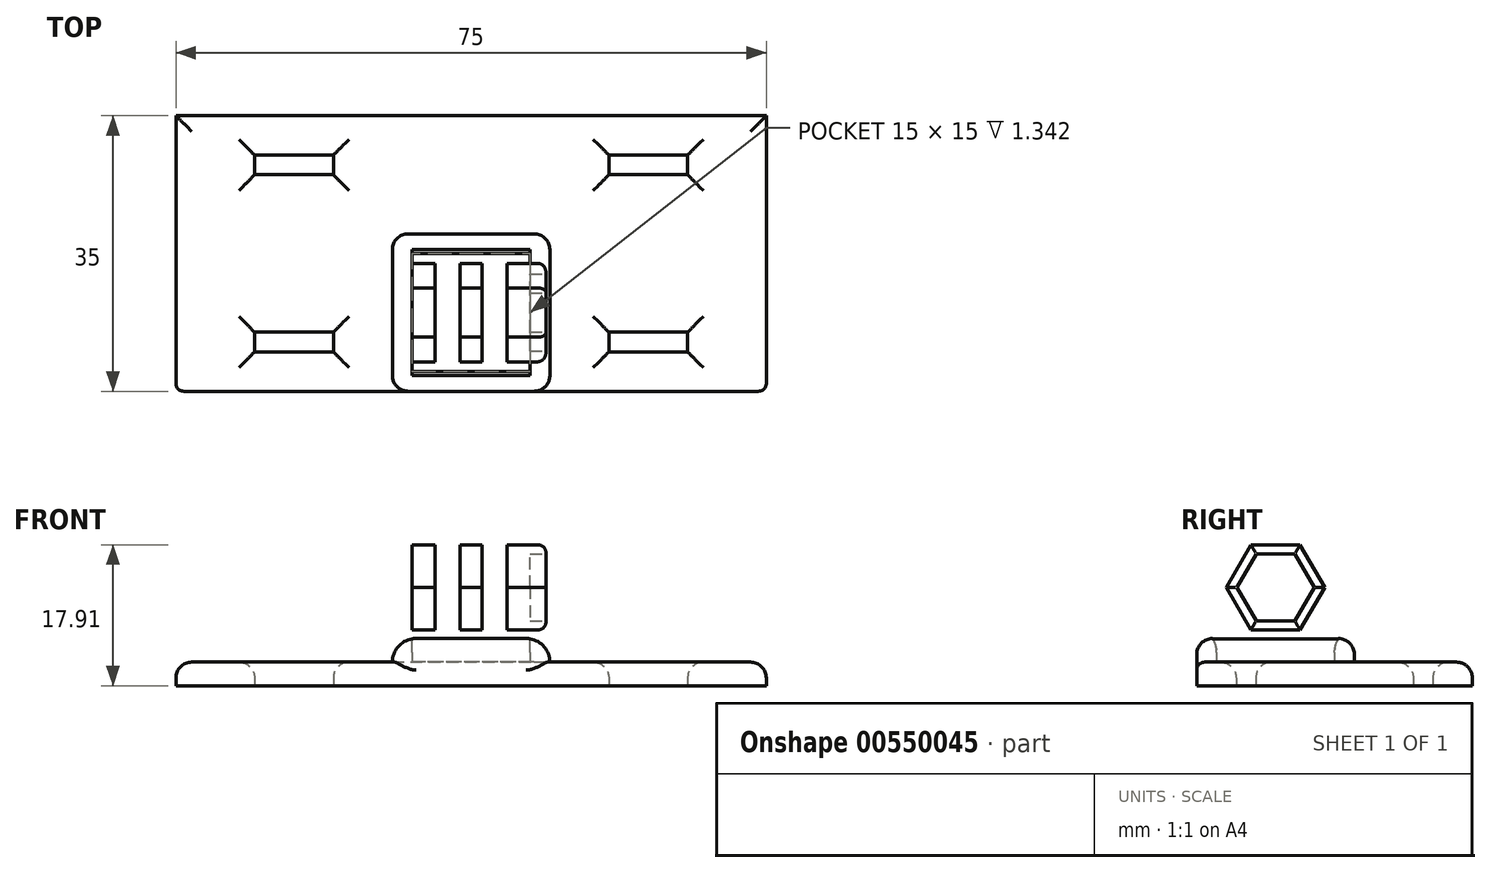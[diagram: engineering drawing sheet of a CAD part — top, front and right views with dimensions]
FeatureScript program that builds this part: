
annotation { "Feature Type Name" : "Feature", "Feature Type Description" : "" }
export const myFeature = defineFeature(function(context is Context, id is Id, definition is map)
    precondition{}
    {
        {
            var Q0;
            Q0=qCreatedBy(makeId("Right.planeOp"),FACE);
            var sketch = newSketch(context, id + "F0", { "sketchPlane" : qUnion([Q0])});
            skPoint(sketch, "E0", {"position": v(0, 12.5) * mm});
            skPoint(sketch, "E1", {"position": v(7.5, 0) * mm});
            skPoint(sketch, "E2.end.orphan", {"position": v(-7.5, 0) * mm});
            skLineSegment(sketch, "E3.top", {"start": v(-7.5, 0) * mm, "end": v(7.5, 0) * mm});
            skLineSegment(sketch, "E3.left", {"start": v(-7.5, 12.5) * mm, "end": v(-7.5, 0) * mm});
            skLineSegment(sketch, "E3.right", {"start": v(7.5, 12.5) * mm, "end": v(7.5, 0) * mm});
            skArc(sketch, "E4", {"start": v(7.5, 12.5) * mm, "mid": v(0, 20) * mm, "end": v(-7.5, 12.5) * mm});
            skCircle(sketch, "E5.cCircle", {"center": v(0, 12.5) * mm, "radius": 4.25 * mm, "construction": true});
            skLineSegment(sketch, "E5.0", {"start": v(-2.45, 16.75) * mm, "end": v(2.45, 16.75) * mm});
            skLineSegment(sketch, "E5.1", {"start": v(2.45, 16.75) * mm, "end": v(4.9, 12.5) * mm});
            skLineSegment(sketch, "E5.2", {"start": v(4.9, 12.5) * mm, "end": v(2.45, 8.25) * mm});
            skLineSegment(sketch, "E5.3", {"start": v(2.45, 8.25) * mm, "end": v(-2.45, 8.25) * mm});
            skLineSegment(sketch, "E5.4", {"start": v(-2.45, 8.25) * mm, "end": v(-4.9, 12.5) * mm});
            skLineSegment(sketch, "E5.5", {"start": v(-4.9, 12.5) * mm, "end": v(-2.45, 16.75) * mm});
            skPoint(sketch, "E5.0.midPoint", {"position": v(0, 16.75) * mm});
            skCircle(sketch, "E6.cCircle", {"center": v(0, 12.5) * mm, "radius": 5.41 * mm, "construction": true});
            skLineSegment(sketch, "E6.0", {"start": v(-3.12, 17.91) * mm, "end": v(3.12, 17.91) * mm});
            skLineSegment(sketch, "E6.1", {"start": v(3.12, 17.91) * mm, "end": v(6.25, 12.5) * mm});
            skLineSegment(sketch, "E6.2", {"start": v(6.25, 12.5) * mm, "end": v(3.12, 7.09) * mm});
            skLineSegment(sketch, "E6.3", {"start": v(3.13, 7.09) * mm, "end": v(-3.12, 7.09) * mm});
            skLineSegment(sketch, "E6.4", {"start": v(-3.12, 7.09) * mm, "end": v(-6.25, 12.5) * mm});
            skLineSegment(sketch, "E6.5", {"start": v(-6.25, 12.5) * mm, "end": v(-3.12, 17.91) * mm});
            skPoint(sketch, "E6.0.midPoint", {"position": v(0, 17.91) * mm});
            skLineSegment(sketch, "E7.top", {"start": v(-7.5, 3) * mm, "end": v(7.5, 3) * mm});
            skLineSegment(sketch, "E7.left", {"start": v(-7.5, 0) * mm, "end": v(-7.5, 3) * mm});
            skLineSegment(sketch, "E7.right", {"start": v(7.5, 0) * mm, "end": v(7.5, 3) * mm});
            skSolve(sketch);
        }
        {
            var Q0;
            Q0=makeQuery(id+"F0.imprint","IMPRINT",FACE,{"disambiguationData":[TD([[makeQuery(id+"F0.imprint","IMPRINT",EDGE,{"derivedFrom":sQuery(id+"F0.wireOp",EDGE,"E3.top")}),1.0]])]});
            extrude(context, id + "F1", {"entities" : qUnion([Q0]), "oppositeDirection" : true, "depth" : 15 * mm, "offsetDistance" : 25 * mm});
        }
        {
            var Q0;
            Q0=makeQuery(id+"F0.imprint","IMPRINT",FACE,{"disambiguationData":[TD([[makeQuery(id+"F0.imprint","IMPRINT",EDGE,{"derivedFrom":sQuery(id+"F0.wireOp",EDGE,"E3.left")}),1.0]])]});
            extrude(context, id + "F2", {"entities" : qUnion([Q0]), "operationType" : NewBodyOperationType.ADD, "oppositeDirection" : true, "depth" : 3 * mm, "offsetDistance" : 25 * mm});
        }
        {
            var Q0;
            Q0=makeQuery(id+"F0.imprint","IMPRINT",FACE,{"disambiguationData":[TD([[makeQuery(id+"F0.imprint","IMPRINT",EDGE,{"derivedFrom":sQuery(id+"F0.wireOp",EDGE,"E5.0")}),1.0]])]});
            extrude(context, id + "F3", {"entities" : qUnion([Q0]), "operationType" : NewBodyOperationType.ADD, "oppositeDirection" : true, "depth" : 3 * mm, "offsetDistance" : 25 * mm});
        }
        {
            var Q0;
            Q0=makeQuery(id+"F0.imprint","IMPRINT",FACE,{"disambiguationData":[TD([[makeQuery(id+"F0.imprint","IMPRINT",EDGE,{"derivedFrom":sQuery(id+"F0.wireOp",EDGE,"E5.0")}),1.0]])]});
            extrude(context, id + "F4", {"entities" : qUnion([Q0]), "operationType" : NewBodyOperationType.ADD, "depth" : 2 * mm, "offsetDistance" : 25 * mm});
        }
        {
            var Q0;
            Q0=makeQuery(id+"F0.imprint","IMPRINT",FACE,{"disambiguationData":[TD([[makeQuery(id+"F0.imprint","IMPRINT",EDGE,{"derivedFrom":sQuery(id+"F0.wireOp",EDGE,"E5.0")}),-1.0]])]});
            extrude(context, id + "F5", {"entities" : qUnion([Q0]), "operationType" : NewBodyOperationType.ADD, "oppositeDirection" : true, "depth" : 3 * mm, "offsetDistance" : 25 * mm});
        }
        {
            var Q0;
            {var subQ0=sQuery(id+"F0.wireOp",EDGE,"E5.5");var subQ1=sQuery(id+"F0.wireOp",EDGE,"E5.4");var subQ2=sQuery(id+"F0.wireOp",EDGE,"E5.3");var subQ3=sQuery(id+"F0.wireOp",EDGE,"E5.2");var subQ4=sQuery(id+"F0.wireOp",EDGE,"E5.1");var subQ5=sQuery(id+"F0.wireOp",EDGE,"E5.0");var subQ6=sQuery(id+"F0.wireOp",EDGE,"E6.5");var subQ7=sQuery(id+"F0.wireOp",EDGE,"E6.4");var subQ8=sQuery(id+"F0.wireOp",EDGE,"E6.3");var subQ9=sQuery(id+"F0.wireOp",EDGE,"E6.2");var subQ10=sQuery(id+"F0.wireOp",EDGE,"E6.1");var subQ11=sQuery(id+"F0.wireOp",EDGE,"E6.0");Q0=makeQuery(id+"F5.boolean.opBoolean","MERGE",FACE,{"derivedFrom":[makeQuery(id+"F3.boolean.opBoolean","MERGE",FACE,{"derivedFrom":[makeQuery(id+"F2.opExtrude","CAP_FACE",FACE,{"disambiguationData":[OSD([sQuery(id+"F0.wireOp",EDGE,"E3.left"),sQuery(id+"F0.wireOp",EDGE,"E3.right"),sQuery(id+"F0.wireOp",EDGE,"E4"),subQ11,subQ10,subQ9,subQ8,subQ7,subQ6,sQuery(id+"F0.wireOp",EDGE,"E7.top")])],"isStart":false}),makeQuery(id+"F3.opExtrude","CAP_FACE",FACE,{"disambiguationData":[OSD([subQ5,subQ4,subQ3,subQ2,subQ1,subQ0,subQ11,subQ10,subQ9,subQ8,subQ7,subQ6])],"isStart":false})]}),makeQuery(id+"F5.opExtrude","CAP_FACE",FACE,{"disambiguationData":[OSD([subQ5,subQ4,subQ3,subQ2,subQ1,subQ0])],"isStart":false})]});}
            extrude(context, id + "F6", {"entities" : qUnion([Q0]), "operationType" : NewBodyOperationType.ADD, "depth" : 12 * mm, "offsetDistance" : 25 * mm});
        }
        {
            var Q0;
            Q0=sQuery(id+"F0.wireOp",VERTEX,"E0");
            var Q1;
            Q1=makeQuery(id+"F1.opExtrude","SWEPT_BODY",BODY,{"disambiguationData":[OSD([sQuery(id+"F0.wireOp",EDGE,"E3.top"),sQuery(id+"F0.wireOp",EDGE,"E7.top"),sQuery(id+"F0.wireOp",EDGE,"E7.left"),sQuery(id+"F0.wireOp",EDGE,"E7.right")])]});
            hole(context, id + "F7", {"style" : HoleStyle.SIMPLE, "endStyle" : HoleEndStyle.BLIND, "holeDiameter" : 5 * mm, "holeDepth" : 15 * mm, "locations" : qUnion([Q0]), "scope" : qUnion([Q1])});
        }
        {
            var Q0;
            Q0=qCreatedBy(makeId("Top.planeOp"),FACE);
            cPlane(context, id + "F8", {"entities" : qUnion([Q0]), "cplaneType" : CPlaneType.OFFSET, "offset" : 20 * mm, "width" : 150 * mm, "height" : 150 * mm});
        }
        {
            var Q0;
            Q0=qCreatedBy(id+"F8.planeOp",FACE);
            var sketch = newSketch(context, id + "F9", { "sketchPlane" : qUnion([Q0])});
            skLineSegment(sketch, "E8.top", {"start": v(0, 7.5) * mm, "end": v(-15, 7.5) * mm});
            skLineSegment(sketch, "E8.left", {"start": v(0, 0) * mm, "end": v(0, 7.5) * mm});
            skLineSegment(sketch, "E8.right", {"start": v(-15, 0) * mm, "end": v(-15, 7.5) * mm});
            skLineSegment(sketch, "E9.top", {"start": v(-15, -7.5) * mm, "end": v(0, -7.5) * mm});
            skLineSegment(sketch, "E9.left", {"start": v(-15, 0) * mm, "end": v(-15, -7.5) * mm});
            skLineSegment(sketch, "E9.right", {"start": v(0, 0) * mm, "end": v(0, -7.5) * mm});
            skLineSegment(sketch, "E10", {"start": v(-7.5, -7.5) * mm, "end": v(-7.5, 7.5) * mm, "construction": true});
            skPoint(sketch, "E11", {"position": v(-6.1, -7.5) * mm});
            skLineSegment(sketch, "E12.bottom", {"start": v(-6.1, -7.5) * mm, "end": v(-8.9, -7.5) * mm});
            skLineSegment(sketch, "E12.top", {"start": v(-6.1, 7.5) * mm, "end": v(-8.9, 7.5) * mm});
            skLineSegment(sketch, "E12.left", {"start": v(-6.1, -7.5) * mm, "end": v(-6.1, 7.5) * mm});
            skLineSegment(sketch, "E12.right", {"start": v(-8.9, -7.5) * mm, "end": v(-8.9, 7.5) * mm});
            skLineSegment(sketch, "E13.bottom", {"start": v(-15, -7.5) * mm, "end": v(-12.05, -7.5) * mm});
            skLineSegment(sketch, "E13.top", {"start": v(-15, 7.5) * mm, "end": v(-12.05, 7.5) * mm});
            skLineSegment(sketch, "E13.left", {"start": v(-15, -7.5) * mm, "end": v(-15, 7.5) * mm});
            skLineSegment(sketch, "E13.right", {"start": v(-12.05, -7.5) * mm, "end": v(-12.05, 7.5) * mm});
            skLineSegment(sketch, "E14.bottom", {"start": v(0, -7.5) * mm, "end": v(-2.95, -7.5) * mm});
            skLineSegment(sketch, "E14.top", {"start": v(0, 7.5) * mm, "end": v(-2.95, 7.5) * mm});
            skLineSegment(sketch, "E14.left", {"start": v(0, -7.5) * mm, "end": v(0, 7.5) * mm});
            skLineSegment(sketch, "E14.right", {"start": v(-2.95, -7.5) * mm, "end": v(-2.95, 7.5) * mm});
            skLineSegment(sketch, "E15", {"start": v(-12.05, -7.5) * mm, "end": v(-8.9, -7.5) * mm, "construction": true});
            skSolve(sketch);
        }
        {
            var Q0;
            {var subQ2=sQuery(id+"F9.wireOp",EDGE,"E12.right");Q0=makeQuery(id+"F9.imprint","IMPRINT",FACE,{"disambiguationData":[TD([[makeQuery(id+"F9.imprint","IMPRINT",EDGE,{"derivedFrom":subQ2}),1.0]])]});}
            var Q1;
            {var subQ2=sQuery(id+"F9.wireOp",EDGE,"E12.left");Q1=makeQuery(id+"F9.imprint","IMPRINT",FACE,{"disambiguationData":[TD([[makeQuery(id+"F9.imprint","IMPRINT",EDGE,{"derivedFrom":subQ2}),-1.0]])]});}
            extrude(context, id + "F10", {"entities" : qUnion([Q0, Q1]), "operationType" : NewBodyOperationType.REMOVE, "oppositeDirection" : true, "depth" : 17 * mm, "offsetDistance" : 25 * mm});
        }
        {
            var Q0;
            Q0=makeQuery(id+"F4.opExtrude","CAP_EDGE",EDGE,{"disambiguationData":[OSD([sQuery(id+"F0.wireOp",EDGE,"E6.4")])],"isStart":false});
            var Q1;
            Q1=makeQuery(id+"F4.opExtrude","CAP_EDGE",EDGE,{"disambiguationData":[OSD([sQuery(id+"F0.wireOp",EDGE,"E6.3")])],"isStart":false});
            var Q2;
            Q2=makeQuery(id+"F4.opExtrude","CAP_EDGE",EDGE,{"disambiguationData":[OSD([sQuery(id+"F0.wireOp",EDGE,"E6.5")])],"isStart":false});
            var Q3;
            Q3=makeQuery(id+"F4.opExtrude","CAP_EDGE",EDGE,{"disambiguationData":[OSD([sQuery(id+"F0.wireOp",EDGE,"E6.0")])],"isStart":false});
            var Q4;
            Q4=makeQuery(id+"F4.opExtrude","CAP_EDGE",EDGE,{"disambiguationData":[OSD([sQuery(id+"F0.wireOp",EDGE,"E6.1")])],"isStart":false});
            var Q5;
            Q5=makeQuery(id+"F4.opExtrude","CAP_EDGE",EDGE,{"disambiguationData":[OSD([sQuery(id+"F0.wireOp",EDGE,"E6.2")])],"isStart":false});
            fillet(context, id + "F11", {"entities" : qUnion([Q0, Q1, Q2, Q3, Q4, Q5]), "radius" : 1 * mm, "tangentPropagation" : true, "allowEdgeOverflow" : false});
        }
        {
            var Q0;
            Q0=makeQuery(id+"F1.opExtrude","SWEPT_FACE",FACE,{"disambiguationData":[OSD([sQuery(id+"F0.wireOp",EDGE,"E3.top")])]});
            var sketch = newSketch(context, id + "F12", { "sketchPlane" : qUnion([Q0])});
            skLineSegment(sketch, "E16", {"start": v(0, 0) * mm, "end": v(-15, 0) * mm, "construction": true});
            skLineSegment(sketch, "E17.bottom", {"start": v(-7.5, 0) * mm, "end": v(30, 0) * mm});
            skLineSegment(sketch, "E17.top", {"start": v(-7.5, -25) * mm, "end": v(30, -25) * mm});
            skLineSegment(sketch, "E17.left", {"start": v(-7.5, 0) * mm, "end": v(-7.5, -25) * mm, "construction": true});
            skLineSegment(sketch, "E17.right", {"start": v(30, 0) * mm, "end": v(30, -25) * mm});
            skLineSegment(sketch, "E18.bottom", {"start": v(-7.5, 0) * mm, "end": v(30, 0) * mm, "construction": true});
            skLineSegment(sketch, "E18.top", {"start": v(-7.5, 10) * mm, "end": v(30, 10) * mm});
            skLineSegment(sketch, "E18.left", {"start": v(-7.5, 0) * mm, "end": v(-7.5, 10) * mm});
            skLineSegment(sketch, "E18.right", {"start": v(30, 0) * mm, "end": v(30, 10) * mm});
            skLineSegment(sketch, "E19.bottom", {"start": v(-7.5, 0) * mm, "end": v(-45, 0) * mm, "construction": true});
            skLineSegment(sketch, "E19.top", {"start": v(-7.5, 10) * mm, "end": v(-45, 10) * mm});
            skLineSegment(sketch, "E19.left", {"start": v(-7.5, 0) * mm, "end": v(-7.5, 10) * mm, "construction": true});
            skLineSegment(sketch, "E19.right", {"start": v(-45, 0) * mm, "end": v(-45, 10) * mm});
            skLineSegment(sketch, "E20.bottom", {"start": v(-7.5, 0) * mm, "end": v(-45, 0) * mm});
            skLineSegment(sketch, "E20.top", {"start": v(-7.5, -25) * mm, "end": v(-45, -25) * mm});
            skLineSegment(sketch, "E20.left", {"start": v(-7.5, 0) * mm, "end": v(-7.5, -25) * mm});
            skLineSegment(sketch, "E20.right", {"start": v(-45, 0) * mm, "end": v(-45, -25) * mm});
            skLineSegment(sketch, "E21", {"start": v(-45, -25) * mm, "end": v(-45, 10) * mm, "construction": true});
            skLineSegment(sketch, "E22", {"start": v(30, 10) * mm, "end": v(-45, 10) * mm, "construction": true});
            skLineSegment(sketch, "E23.bottom", {"start": v(-35, 2.5) * mm, "end": v(-25, 2.5) * mm});
            skLineSegment(sketch, "E23.top", {"start": v(-35, 5) * mm, "end": v(-25, 5) * mm});
            skLineSegment(sketch, "E23.left", {"start": v(-35, 2.5) * mm, "end": v(-35, 5) * mm});
            skLineSegment(sketch, "E23.right", {"start": v(-25, 2.5) * mm, "end": v(-25, 5) * mm});
            skLineSegment(sketch, "E24.bottom", {"start": v(10, 2.5) * mm, "end": v(20, 2.5) * mm});
            skLineSegment(sketch, "E24.top", {"start": v(10, 5) * mm, "end": v(20, 5) * mm});
            skLineSegment(sketch, "E24.left", {"start": v(10, 2.5) * mm, "end": v(10, 5) * mm});
            skLineSegment(sketch, "E24.right", {"start": v(20, 2.5) * mm, "end": v(20, 5) * mm});
            skLineSegment(sketch, "E25.bottom", {"start": v(10, -20) * mm, "end": v(20, -20) * mm});
            skLineSegment(sketch, "E25.top", {"start": v(10, -17.5) * mm, "end": v(20, -17.5) * mm});
            skLineSegment(sketch, "E25.left", {"start": v(10, -20) * mm, "end": v(10, -17.5) * mm});
            skLineSegment(sketch, "E25.right", {"start": v(20, -20) * mm, "end": v(20, -17.5) * mm});
            skLineSegment(sketch, "E26.bottom", {"start": v(-35, -20) * mm, "end": v(-25, -20) * mm});
            skLineSegment(sketch, "E26.top", {"start": v(-35, -17.5) * mm, "end": v(-25, -17.5) * mm});
            skLineSegment(sketch, "E26.left", {"start": v(-35, -20) * mm, "end": v(-35, -17.5) * mm});
            skLineSegment(sketch, "E26.right", {"start": v(-25, -20) * mm, "end": v(-25, -17.5) * mm});
            skLineSegment(sketch, "E27", {"start": v(10, -20) * mm, "end": v(10, -25) * mm, "construction": true});
            skLineSegment(sketch, "E28", {"start": v(-25, -20) * mm, "end": v(-25, -25) * mm, "construction": true});
            skLineSegment(sketch, "E29", {"start": v(10, 5) * mm, "end": v(10, 10) * mm, "construction": true});
            skLineSegment(sketch, "E30", {"start": v(-25, 5) * mm, "end": v(-25, 10) * mm, "construction": true});
            skLineSegment(sketch, "E31", {"start": v(20, -20) * mm, "end": v(30, -20) * mm, "construction": true});
            skLineSegment(sketch, "E32", {"start": v(20, 5) * mm, "end": v(30, 5) * mm, "construction": true});
            skLineSegment(sketch, "E33", {"start": v(-35, 5) * mm, "end": v(-45, 5) * mm, "construction": true});
            skLineSegment(sketch, "E34", {"start": v(-35, -17.5) * mm, "end": v(-45, -17.5) * mm, "construction": true});
            skSolve(sketch);
        }
        {
            var Q0;
            Q0 = qSketchRegion(id + "F12", true);
            extrude(context, id + "F13", {"entities" : qUnion([Q0]), "operationType" : NewBodyOperationType.ADD, "oppositeDirection" : true, "depth" : 3 * mm, "offsetDistance" : 25 * mm});
        }
        {
            var Q0;
            {var subQ0=sQuery(id+"F9.wireOp",EDGE,"E9.top");var subQ1=sQuery(id+"F9.wireOp",EDGE,"E8.top");Q0=makeQuery(id+"F13.boolean.opBoolean","MERGE",FACE,{"derivedFrom":[makeQuery(id+"F10.boolean.opBoolean","COPY",FACE,{"derivedFrom":makeQuery(id+"F10.opExtrude","CAP_FACE",FACE,{"disambiguationData":[OSD([subQ1,subQ0,sQuery(id+"F9.wireOp",EDGE,"E12.left"),sQuery(id+"F9.wireOp",EDGE,"E14.right")])],"isStart":false})}),makeQuery(id+"F10.boolean.opBoolean","COPY",FACE,{"derivedFrom":makeQuery(id+"F10.opExtrude","CAP_FACE",FACE,{"disambiguationData":[OSD([subQ1,subQ0,sQuery(id+"F9.wireOp",EDGE,"E12.right"),sQuery(id+"F9.wireOp",EDGE,"E13.right")])],"isStart":false})}),makeQuery(id+"F13.opExtrude","CAP_FACE",FACE,{"disambiguationData":[OSD([sQuery(id+"F12.wireOp",EDGE,"E17.top"),sQuery(id+"F12.wireOp",EDGE,"E17.right"),sQuery(id+"F12.wireOp",EDGE,"E18.top"),sQuery(id+"F12.wireOp",EDGE,"E18.right"),sQuery(id+"F12.wireOp",EDGE,"E19.top"),sQuery(id+"F12.wireOp",EDGE,"E19.right"),sQuery(id+"F12.wireOp",EDGE,"E20.top"),sQuery(id+"F12.wireOp",EDGE,"E20.right"),sQuery(id+"F12.wireOp",EDGE,"E23.bottom"),sQuery(id+"F12.wireOp",EDGE,"E23.top"),sQuery(id+"F12.wireOp",EDGE,"E23.left"),sQuery(id+"F12.wireOp",EDGE,"E23.right"),sQuery(id+"F12.wireOp",EDGE,"E24.bottom"),sQuery(id+"F12.wireOp",EDGE,"E24.top"),sQuery(id+"F12.wireOp",EDGE,"E24.left"),sQuery(id+"F12.wireOp",EDGE,"E24.right"),sQuery(id+"F12.wireOp",EDGE,"E25.bottom"),sQuery(id+"F12.wireOp",EDGE,"E25.top"),sQuery(id+"F12.wireOp",EDGE,"E25.left"),sQuery(id+"F12.wireOp",EDGE,"E25.right"),sQuery(id+"F12.wireOp",EDGE,"E26.bottom"),sQuery(id+"F12.wireOp",EDGE,"E26.top"),sQuery(id+"F12.wireOp",EDGE,"E26.left"),sQuery(id+"F12.wireOp",EDGE,"E26.right"),sQuery(id+"F12.wireOp",EDGE,"uoogrX0K-hDYU-zlST-xG9k-PASHNL5tbvwQ.bottom"),sQuery(id+"F12.wireOp",EDGE,"uoogrX0K-hDYU-zlST-xG9k-PASHNL5tbvwQ.top"),sQuery(id+"F12.wireOp",EDGE,"uoogrX0K-hDYU-zlST-xG9k-PASHNL5tbvwQ.left"),sQuery(id+"F12.wireOp",EDGE,"uoogrX0K-hDYU-zlST-xG9k-PASHNL5tbvwQ.right"),sQuery(id+"F12.wireOp",EDGE,"PsY2hvwu-Xq4P-Rnf6-JxBB-JTYvY8m7WrV5.bottom"),sQuery(id+"F12.wireOp",EDGE,"PsY2hvwu-Xq4P-Rnf6-JxBB-JTYvY8m7WrV5.top"),sQuery(id+"F12.wireOp",EDGE,"PsY2hvwu-Xq4P-Rnf6-JxBB-JTYvY8m7WrV5.left"),sQuery(id+"F12.wireOp",EDGE,"PsY2hvwu-Xq4P-Rnf6-JxBB-JTYvY8m7WrV5.right")])],"isStart":false})]});}
            var sketch = newSketch(context, id + "F14", { "sketchPlane" : qUnion([Q0])});
            skLineSegment(sketch, "E35.bottom", {"start": v(2.5, 10) * mm, "end": v(-2.95, 10) * mm});
            skLineSegment(sketch, "E35.top", {"start": v(2.5, 7.5) * mm, "end": v(-2.95, 7.5) * mm});
            skLineSegment(sketch, "E35.left", {"start": v(2.5, 10) * mm, "end": v(2.5, 7.5) * mm});
            skLineSegment(sketch, "E35.right", {"start": v(-2.95, 10) * mm, "end": v(-2.95, 7.5) * mm});
            skLineSegment(sketch, "E36.bottom", {"start": v(-6.1, 7.5) * mm, "end": v(-8.9, 7.5) * mm});
            skLineSegment(sketch, "E36.top", {"start": v(-6.1, 10) * mm, "end": v(-8.9, 10) * mm});
            skLineSegment(sketch, "E36.left", {"start": v(-6.1, 7.5) * mm, "end": v(-6.1, 10) * mm});
            skLineSegment(sketch, "E36.right", {"start": v(-8.9, 7.5) * mm, "end": v(-8.9, 10) * mm});
            skLineSegment(sketch, "E37.bottom", {"start": v(-12.05, 10) * mm, "end": v(-17.5, 10) * mm});
            skLineSegment(sketch, "E37.top", {"start": v(-12.05, 7.5) * mm, "end": v(-17.5, 7.5) * mm});
            skLineSegment(sketch, "E37.left", {"start": v(-12.05, 10) * mm, "end": v(-12.05, 7.5) * mm});
            skLineSegment(sketch, "E37.right", {"start": v(-17.5, 10) * mm, "end": v(-17.5, 7.5) * mm});
            skLineSegment(sketch, "E38", {"start": v(-12.05, 10) * mm, "end": v(-8.9, 10) * mm, "construction": true});
            skLineSegment(sketch, "E39.bottom", {"start": v(2.5, 7.5) * mm, "end": v(0, 7.5) * mm});
            skLineSegment(sketch, "E39.top", {"start": v(2.5, -7.5) * mm, "end": v(0, -7.5) * mm});
            skLineSegment(sketch, "E39.left", {"start": v(2.5, 7.5) * mm, "end": v(2.5, -7.5) * mm});
            skLineSegment(sketch, "E39.right", {"start": v(0, 7.5) * mm, "end": v(0, -7.5) * mm});
            skLineSegment(sketch, "E40.bottom", {"start": v(-17.5, 7.5) * mm, "end": v(-15, 7.5) * mm});
            skLineSegment(sketch, "E40.top", {"start": v(-17.5, -7.5) * mm, "end": v(-15, -7.5) * mm});
            skLineSegment(sketch, "E40.left", {"start": v(-17.5, 7.5) * mm, "end": v(-17.5, -7.5) * mm});
            skLineSegment(sketch, "E40.right", {"start": v(-15, 7.5) * mm, "end": v(-15, -7.5) * mm});
            skLineSegment(sketch, "E41.bottom", {"start": v(-17.5, -7.5) * mm, "end": v(-12.05, -7.5) * mm});
            skLineSegment(sketch, "E41.top", {"start": v(-17.5, -10) * mm, "end": v(-12.05, -10) * mm});
            skLineSegment(sketch, "E41.left", {"start": v(-17.5, -7.5) * mm, "end": v(-17.5, -10) * mm});
            skLineSegment(sketch, "E41.right", {"start": v(-12.05, -7.5) * mm, "end": v(-12.05, -10) * mm});
            skLineSegment(sketch, "E42.bottom", {"start": v(2.5, -7.5) * mm, "end": v(-2.95, -7.5) * mm});
            skLineSegment(sketch, "E42.top", {"start": v(2.5, -10) * mm, "end": v(-2.95, -10) * mm});
            skLineSegment(sketch, "E42.left", {"start": v(2.5, -7.5) * mm, "end": v(2.5, -10) * mm});
            skLineSegment(sketch, "E42.right", {"start": v(-2.95, -7.5) * mm, "end": v(-2.95, -10) * mm});
            skLineSegment(sketch, "E43.bottom", {"start": v(-6.1, -7.5) * mm, "end": v(-8.9, -7.5) * mm});
            skLineSegment(sketch, "E43.top", {"start": v(-6.1, -10) * mm, "end": v(-8.9, -10) * mm});
            skLineSegment(sketch, "E43.left", {"start": v(-6.1, -7.5) * mm, "end": v(-6.1, -10) * mm});
            skLineSegment(sketch, "E43.right", {"start": v(-8.9, -7.5) * mm, "end": v(-8.9, -10) * mm});
            skLineSegment(sketch, "E44", {"start": v(-12.05, -8.75) * mm, "end": v(-8.9, -8.75) * mm, "construction": true});
            skLineSegment(sketch, "E45.bottom", {"start": v(-2.95, 7.5) * mm, "end": v(-6.1, 7.5) * mm});
            skLineSegment(sketch, "E45.top", {"start": v(-2.95, 10) * mm, "end": v(-6.1, 10) * mm});
            skLineSegment(sketch, "E45.left", {"start": v(-2.95, 7.5) * mm, "end": v(-2.95, 10) * mm});
            skLineSegment(sketch, "E46.bottom", {"start": v(-8.9, 7.5) * mm, "end": v(-12.05, 7.5) * mm});
            skLineSegment(sketch, "E46.top", {"start": v(-8.9, 10) * mm, "end": v(-12.05, 10) * mm});
            skLineSegment(sketch, "E46.right", {"start": v(-12.05, 7.5) * mm, "end": v(-12.05, 10) * mm});
            skLineSegment(sketch, "E47.bottom", {"start": v(-2.95, -10) * mm, "end": v(-6.1, -10) * mm});
            skLineSegment(sketch, "E47.top", {"start": v(-2.95, -7.5) * mm, "end": v(-6.1, -7.5) * mm});
            skLineSegment(sketch, "E47.left", {"start": v(-2.95, -10) * mm, "end": v(-2.95, -7.5) * mm});
            skLineSegment(sketch, "E47.right", {"start": v(-6.1, -10) * mm, "end": v(-6.1, -7.5) * mm});
            skLineSegment(sketch, "E48.bottom", {"start": v(-8.9, -10) * mm, "end": v(-12.05, -10) * mm});
            skLineSegment(sketch, "E48.top", {"start": v(-8.9, -7.5) * mm, "end": v(-12.05, -7.5) * mm});
            skLineSegment(sketch, "E48.left", {"start": v(-8.9, -10) * mm, "end": v(-8.9, -7.5) * mm});
            skLineSegment(sketch, "E48.right", {"start": v(-12.05, -10) * mm, "end": v(-12.05, -7.5) * mm});
            skLineSegment(sketch, "E49", {"start": v(-6.1, -7.5) * mm, "end": v(-2.95, -7.5) * mm});
            skLineSegment(sketch, "E50", {"start": v(-12.05, -7.5) * mm, "end": v(-8.9, -7.5) * mm});
            skLineSegment(sketch, "E51", {"start": v(-12.05, 7.5) * mm, "end": v(-8.9, 7.5) * mm});
            skLineSegment(sketch, "E52", {"start": v(-6.1, 7.5) * mm, "end": v(-2.95, 7.5) * mm});
            skSolve(sketch);
        }
        {
            var Q0;
            Q0 = qSketchRegion(id + "F14", true);
            extrude(context, id + "F15", {"entities" : qUnion([Q0]), "operationType" : NewBodyOperationType.ADD, "depth" : 3 * mm, "offsetDistance" : 25 * mm});
        }
        {
            var Q0;
            Q0=makeQuery(id+"F15.opExtrude","CAP_EDGE",EDGE,{"disambiguationData":[OSD([sQuery(id+"F14.wireOp",EDGE,"E35.left"),sQuery(id+"F14.wireOp",EDGE,"E39.left"),sQuery(id+"F14.wireOp",EDGE,"E42.left")])],"isStart":false});
            var Q1;
            Q1=makeQuery(id+"F15.opExtrude","CAP_EDGE",EDGE,{"disambiguationData":[OSD([sQuery(id+"F14.wireOp",EDGE,"E37.right"),sQuery(id+"F14.wireOp",EDGE,"E40.left"),sQuery(id+"F14.wireOp",EDGE,"E41.left")])],"isStart":false});
            fillet(context, id + "F16", {"entities" : qUnion([Q0, Q1]), "radius" : 3 * mm, "tangentPropagation" : true, "allowEdgeOverflow" : false});
        }
        {
            var Q0;
            Q0=makeQuery(id+"F15.opExtrude","CAP_EDGE",EDGE,{"disambiguationData":[OSD([sQuery(id+"F14.wireOp",EDGE,"E35.bottom")])],"isStart":false});
            var Q1;
            Q1=makeQuery(id+"F15.opExtrude","CAP_EDGE",EDGE,{"disambiguationData":[OSD([sQuery(id+"F14.wireOp",EDGE,"E37.bottom")])],"isStart":false});
            var Q2;
            Q2=makeQuery(id+"F15.opExtrude","CAP_EDGE",EDGE,{"disambiguationData":[OSD([sQuery(id+"F14.wireOp",EDGE,"E41.top")])],"isStart":false});
            var Q3;
            Q3=makeQuery(id+"F15.opExtrude","CAP_EDGE",EDGE,{"disambiguationData":[OSD([sQuery(id+"F14.wireOp",EDGE,"E42.top")])],"isStart":false});
            fillet(context, id + "F17", {"entities" : qUnion([Q0, Q1, Q2, Q3]), "radius" : 2 * mm, "tangentPropagation" : true, "allowEdgeOverflow" : false});
        }
        {
            var Q0;
            {var subQ1=sQuery(id+"F14.wireOp",EDGE,"E50");var subQ2=sQuery(id+"F14.wireOp",EDGE,"E49");var subQ3=sQuery(id+"F14.wireOp",EDGE,"E43.bottom");var subQ4=sQuery(id+"F14.wireOp",EDGE,"E42.bottom");var subQ5=sQuery(id+"F14.wireOp",EDGE,"E41.bottom");var subQ6=makeQuery(id+"F15.opExtrude","CAP_FACE",FACE,{"disambiguationData":[OSD([sQuery(id+"F14.wireOp",EDGE,"E35.bottom"),sQuery(id+"F14.wireOp",EDGE,"E35.top"),sQuery(id+"F14.wireOp",EDGE,"E35.left"),sQuery(id+"F14.wireOp",EDGE,"E36.bottom"),sQuery(id+"F14.wireOp",EDGE,"E36.top"),sQuery(id+"F14.wireOp",EDGE,"E37.bottom"),sQuery(id+"F14.wireOp",EDGE,"E37.top"),sQuery(id+"F14.wireOp",EDGE,"E37.right"),sQuery(id+"F14.wireOp",EDGE,"E39.left"),sQuery(id+"F14.wireOp",EDGE,"E39.right"),sQuery(id+"F14.wireOp",EDGE,"E40.left"),sQuery(id+"F14.wireOp",EDGE,"E40.right"),subQ5,sQuery(id+"F14.wireOp",EDGE,"E41.top"),sQuery(id+"F14.wireOp",EDGE,"E41.left"),subQ4,sQuery(id+"F14.wireOp",EDGE,"E42.top"),sQuery(id+"F14.wireOp",EDGE,"E42.left"),subQ3,sQuery(id+"F14.wireOp",EDGE,"E43.top"),sQuery(id+"F14.wireOp",EDGE,"E45.top"),sQuery(id+"F14.wireOp",EDGE,"E46.top"),sQuery(id+"F14.wireOp",EDGE,"E47.bottom"),sQuery(id+"F14.wireOp",EDGE,"E48.bottom"),subQ2,subQ1,sQuery(id+"F14.wireOp",EDGE,"E51"),sQuery(id+"F14.wireOp",EDGE,"E52")])],"isStart":false});var subQ7=makeQuery(id+"F15.opExtrude","SWEPT_FACE",FACE,{"disambiguationData":[OSD([subQ5,subQ4,subQ3,subQ2,subQ1])]});Q0=makeQuery(id+"F15.boolean.opBoolean","SPLIT",EDGE,{"disambiguationData":[topologyDisambiguationEdgeConnected([subQ6,subQ7]),TD([makeQuery(id+"F10.boolean.opBoolean","COPY",FACE,{"derivedFrom":makeQuery(id+"F10.opExtrude","SWEPT_FACE",FACE,{"disambiguationData":[OSD([sQuery(id+"F9.wireOp",EDGE,"E12.right")])]})})])],"derivedFrom":makeQuery(id+"F15.opExtrude","CAP_EDGE",EDGE,{"disambiguationData":[OSD([subQ5,subQ4,subQ3,subQ2,subQ1])],"isStart":false})});}
            var Q1;
            {var subQ1=sQuery(id+"F14.wireOp",EDGE,"E52");var subQ2=sQuery(id+"F14.wireOp",EDGE,"E51");var subQ3=sQuery(id+"F14.wireOp",EDGE,"E37.top");var subQ4=sQuery(id+"F14.wireOp",EDGE,"E36.bottom");var subQ5=sQuery(id+"F14.wireOp",EDGE,"E35.top");var subQ6=makeQuery(id+"F15.opExtrude","SWEPT_FACE",FACE,{"disambiguationData":[OSD([subQ5,subQ4,subQ3,subQ2,subQ1])]});var subQ7=makeQuery(id+"F15.opExtrude","CAP_FACE",FACE,{"disambiguationData":[OSD([sQuery(id+"F14.wireOp",EDGE,"E35.bottom"),subQ5,sQuery(id+"F14.wireOp",EDGE,"E35.left"),subQ4,sQuery(id+"F14.wireOp",EDGE,"E36.top"),sQuery(id+"F14.wireOp",EDGE,"E37.bottom"),subQ3,sQuery(id+"F14.wireOp",EDGE,"E37.right"),sQuery(id+"F14.wireOp",EDGE,"E39.left"),sQuery(id+"F14.wireOp",EDGE,"E39.right"),sQuery(id+"F14.wireOp",EDGE,"E40.left"),sQuery(id+"F14.wireOp",EDGE,"E40.right"),sQuery(id+"F14.wireOp",EDGE,"E41.bottom"),sQuery(id+"F14.wireOp",EDGE,"E41.top"),sQuery(id+"F14.wireOp",EDGE,"E41.left"),sQuery(id+"F14.wireOp",EDGE,"E42.bottom"),sQuery(id+"F14.wireOp",EDGE,"E42.top"),sQuery(id+"F14.wireOp",EDGE,"E42.left"),sQuery(id+"F14.wireOp",EDGE,"E43.bottom"),sQuery(id+"F14.wireOp",EDGE,"E43.top"),sQuery(id+"F14.wireOp",EDGE,"E45.top"),sQuery(id+"F14.wireOp",EDGE,"E46.top"),sQuery(id+"F14.wireOp",EDGE,"E47.bottom"),sQuery(id+"F14.wireOp",EDGE,"E48.bottom"),sQuery(id+"F14.wireOp",EDGE,"E49"),sQuery(id+"F14.wireOp",EDGE,"E50"),subQ2,subQ1])],"isStart":false});Q1=makeQuery(id+"F15.boolean.opBoolean","SPLIT",EDGE,{"disambiguationData":[topologyDisambiguationEdgeConnected([subQ7,subQ6]),TD([makeQuery(id+"F10.boolean.opBoolean","COPY",FACE,{"derivedFrom":makeQuery(id+"F10.opExtrude","SWEPT_FACE",FACE,{"disambiguationData":[OSD([sQuery(id+"F9.wireOp",EDGE,"E12.right")])]})})])],"derivedFrom":makeQuery(id+"F15.opExtrude","CAP_EDGE",EDGE,{"disambiguationData":[OSD([subQ5,subQ4,subQ3,subQ2,subQ1])],"isStart":false})});}
            fillet(context, id + "F18", {"entities" : qUnion([Q0, Q1]), "radius" : 3 * mm, "tangentPropagation" : true, "allowEdgeOverflow" : false});
        }
        {
            var Q0;
            Q0=makeQuery(id+"F13.opExtrude","CAP_EDGE",EDGE,{"disambiguationData":[OSD([sQuery(id+"F12.wireOp",EDGE,"E17.top"),sQuery(id+"F12.wireOp",EDGE,"E20.top")])],"isStart":false});
            var Q1;
            Q1=makeQuery(id+"F13.opExtrude","CAP_EDGE",EDGE,{"disambiguationData":[OSD([sQuery(id+"F12.wireOp",EDGE,"E19.right"),sQuery(id+"F12.wireOp",EDGE,"E20.right")])],"isStart":false});
            var Q2;
            Q2=makeQuery(id+"F13.opExtrude","CAP_EDGE",EDGE,{"disambiguationData":[OSD([sQuery(id+"F12.wireOp",EDGE,"E23.bottom")])],"isStart":false});
            var Q3;
            Q3=makeQuery(id+"F13.opExtrude","CAP_EDGE",EDGE,{"disambiguationData":[OSD([sQuery(id+"F12.wireOp",EDGE,"E23.left")])],"isStart":false});
            var Q4;
            Q4=makeQuery(id+"F13.opExtrude","CAP_EDGE",EDGE,{"disambiguationData":[OSD([sQuery(id+"F12.wireOp",EDGE,"E23.top")])],"isStart":false});
            var Q5;
            Q5=makeQuery(id+"F13.opExtrude","CAP_EDGE",EDGE,{"disambiguationData":[OSD([sQuery(id+"F12.wireOp",EDGE,"E23.right")])],"isStart":false});
            var Q6;
            Q6=makeQuery(id+"F13.opExtrude","CAP_EDGE",EDGE,{"disambiguationData":[OSD([sQuery(id+"F12.wireOp",EDGE,"E26.bottom")])],"isStart":false});
            var Q7;
            Q7=makeQuery(id+"F13.opExtrude","CAP_EDGE",EDGE,{"disambiguationData":[OSD([sQuery(id+"F12.wireOp",EDGE,"E26.top")])],"isStart":false});
            var Q8;
            Q8=makeQuery(id+"F13.opExtrude","CAP_EDGE",EDGE,{"disambiguationData":[OSD([sQuery(id+"F12.wireOp",EDGE,"E26.left")])],"isStart":false});
            var Q9;
            Q9=makeQuery(id+"F13.opExtrude","CAP_EDGE",EDGE,{"disambiguationData":[OSD([sQuery(id+"F12.wireOp",EDGE,"E26.right")])],"isStart":false});
            var Q10;
            Q10=makeQuery(id+"F13.opExtrude","CAP_EDGE",EDGE,{"disambiguationData":[OSD([sQuery(id+"F12.wireOp",EDGE,"E17.right"),sQuery(id+"F12.wireOp",EDGE,"E18.right")])],"isStart":false});
            var Q11;
            Q11=makeQuery(id+"F13.opExtrude","CAP_EDGE",EDGE,{"disambiguationData":[OSD([sQuery(id+"F12.wireOp",EDGE,"E24.left")])],"isStart":false});
            var Q12;
            Q12=makeQuery(id+"F13.opExtrude","CAP_EDGE",EDGE,{"disambiguationData":[OSD([sQuery(id+"F12.wireOp",EDGE,"E24.top")])],"isStart":false});
            var Q13;
            Q13=makeQuery(id+"F13.opExtrude","CAP_EDGE",EDGE,{"disambiguationData":[OSD([sQuery(id+"F12.wireOp",EDGE,"E24.bottom")])],"isStart":false});
            var Q14;
            Q14=makeQuery(id+"F13.opExtrude","CAP_EDGE",EDGE,{"disambiguationData":[OSD([sQuery(id+"F12.wireOp",EDGE,"E24.right")])],"isStart":false});
            var Q15;
            Q15=makeQuery(id+"F13.opExtrude","CAP_EDGE",EDGE,{"disambiguationData":[OSD([sQuery(id+"F12.wireOp",EDGE,"E25.top")])],"isStart":false});
            var Q16;
            Q16=makeQuery(id+"F13.opExtrude","CAP_EDGE",EDGE,{"disambiguationData":[OSD([sQuery(id+"F12.wireOp",EDGE,"E25.left")])],"isStart":false});
            var Q17;
            Q17=makeQuery(id+"F13.opExtrude","CAP_EDGE",EDGE,{"disambiguationData":[OSD([sQuery(id+"F12.wireOp",EDGE,"E25.bottom")])],"isStart":false});
            var Q18;
            Q18=makeQuery(id+"F13.opExtrude","CAP_EDGE",EDGE,{"disambiguationData":[OSD([sQuery(id+"F12.wireOp",EDGE,"E25.right")])],"isStart":false});
            fillet(context, id + "F19", {"entities" : qUnion([Q0, Q1, Q2, Q3, Q4, Q5, Q6, Q7, Q8, Q9, Q10, Q11, Q12, Q13, Q14, Q15, Q16, Q17, Q18]), "radius" : 2 * mm, "tangentPropagation" : true, "allowEdgeOverflow" : false});
        }
        {
            var Q0;
            {var subQ0=sQuery(id+"F12.wireOp",EDGE,"E19.top");var subQ1=sQuery(id+"F12.wireOp",EDGE,"E18.top");var subQ4=sQuery(id+"F12.wireOp",EDGE,"E20.right");var subQ5=sQuery(id+"F12.wireOp",EDGE,"E19.right");Q0=makeQuery(id+"F15.boolean.opBoolean","SPLIT",EDGE,{"disambiguationData":[TD([makeQuery(id+"F13.opExtrude","SWEPT_FACE",FACE,{"disambiguationData":[OSD([subQ5,subQ4])]})])],"derivedFrom":makeQuery(id+"F13.opExtrude","CAP_EDGE",EDGE,{"disambiguationData":[OSD([subQ1,subQ0])],"isStart":false})});}
            var Q1;
            {var subQ0=sQuery(id+"F12.wireOp",EDGE,"E18.right");var subQ1=sQuery(id+"F12.wireOp",EDGE,"E17.right");var subQ4=sQuery(id+"F12.wireOp",EDGE,"E19.top");var subQ5=sQuery(id+"F12.wireOp",EDGE,"E18.top");Q1=makeQuery(id+"F15.boolean.opBoolean","SPLIT",EDGE,{"disambiguationData":[TD([makeQuery(id+"F13.opExtrude","SWEPT_FACE",FACE,{"disambiguationData":[OSD([subQ1,subQ0])]})])],"derivedFrom":makeQuery(id+"F13.opExtrude","CAP_EDGE",EDGE,{"disambiguationData":[OSD([subQ5,subQ4])],"isStart":false})});}
            fillet(context, id + "F20", {"entities" : qUnion([Q0, Q1]), "radius" : 1 * mm, "tangentPropagation" : true, "allowEdgeOverflow" : false});
        }
    });
